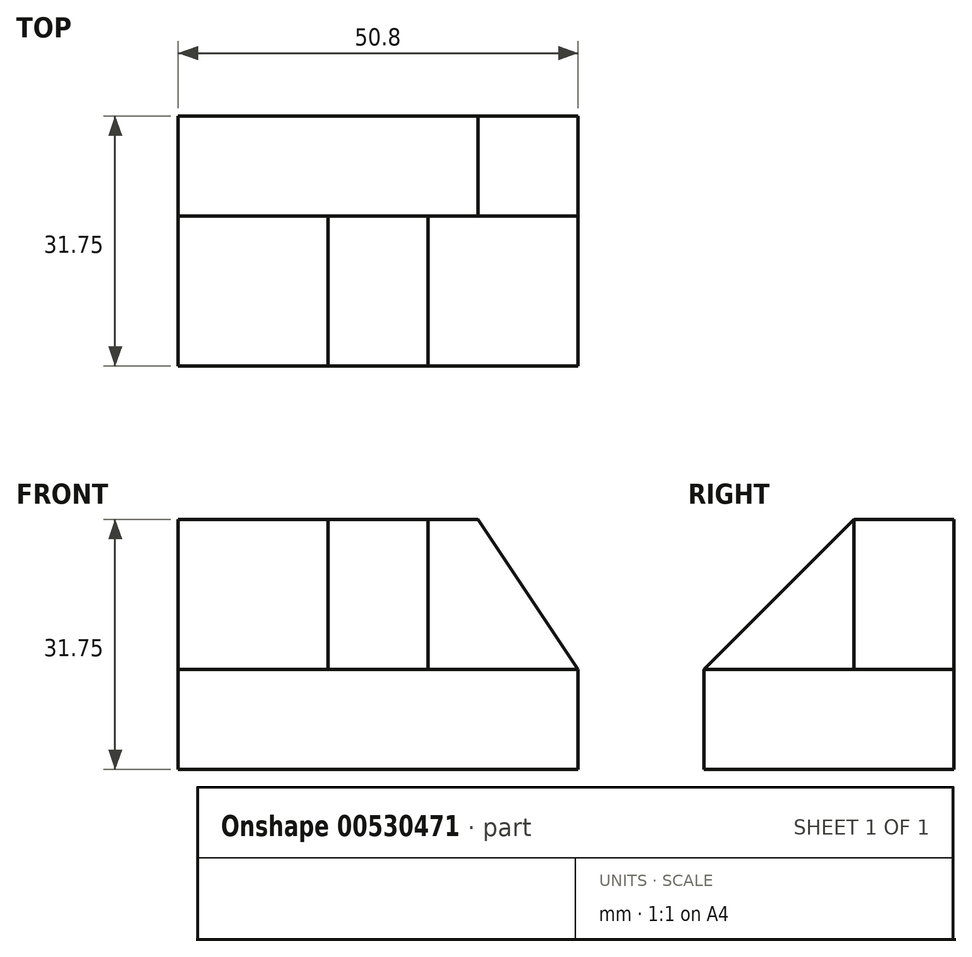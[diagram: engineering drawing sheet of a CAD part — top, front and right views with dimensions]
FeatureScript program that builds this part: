
annotation { "Feature Type Name" : "Feature", "Feature Type Description" : "" }
export const myFeature = defineFeature(function(context is Context, id is Id, definition is map)
    precondition{}
    {
        {
            var Q0;
            Q0=qCreatedBy(makeId("Front.planeOp"),FACE);
            var sketch = newSketch(context, id + "F0", { "sketchPlane" : qUnion([Q0])});
            skLineSegment(sketch, "E0", {"start": v(-85.15, 31.75) * mm, "end": v(-85.15, 0) * mm});
            skLineSegment(sketch, "E1", {"start": v(-85.15, 0) * mm, "end": v(-34.35, 0) * mm});
            skLineSegment(sketch, "E2", {"start": v(-34.35, 0) * mm, "end": v(-34.35, 12.7) * mm});
            skLineSegment(sketch, "E3", {"start": v(-85.15, 31.75) * mm, "end": v(-47.05, 31.75) * mm});
            skLineSegment(sketch, "E4", {"start": v(-47.05, 31.75) * mm, "end": v(-34.35, 12.7) * mm});
            skLineSegment(sketch, "E5", {"start": v(-34.35, 12.7) * mm, "end": v(-85.15, 12.7) * mm});
            skSolve(sketch);
        }
        {
            var Q0;
            {var subQ0=sQuery(id+"F0.wireOp",EDGE,"E1");Q0=makeQuery(id+"F0.imprint","IMPRINT",FACE,{"disambiguationData":[TD([[makeQuery(id+"F0.imprint","IMPRINT",EDGE,{"derivedFrom":subQ0}),1.0]])]});}
            var Q1;
            {var subQ0=sQuery(id+"F0.wireOp",EDGE,"E3");Q1=makeQuery(id+"F0.imprint","IMPRINT",FACE,{"disambiguationData":[TD([[makeQuery(id+"F0.imprint","IMPRINT",EDGE,{"derivedFrom":subQ0}),-1.0]])]});}
            extrude(context, id + "F1", {"entities" : qUnion([Q0, Q1]), "oppositeDirection" : true, "depth" : 31.75 * mm, "offsetDistance" : 25.4 * mm});
        }
        {
            var Q0;
            Q0=makeQuery(id+"F1.opExtrude","CAP_FACE",FACE,{"disambiguationData":[OSD([sQuery(id+"F0.wireOp",EDGE,"E0"),sQuery(id+"F0.wireOp",EDGE,"E1"),sQuery(id+"F0.wireOp",EDGE,"E2"),sQuery(id+"F0.wireOp",EDGE,"E3"),sQuery(id+"F0.wireOp",EDGE,"E4")])],"isStart":true});
            var sketch = newSketch(context, id + "F2", { "sketchPlane" : qUnion([Q0])});
            skLineSegment(sketch, "E6", {"start": v(-34.35, 12.7) * mm, "end": v(-85.15, 12.7) * mm});
            skSolve(sketch);
        }
        {
            var Q0;
            {var subQ0=sQuery(id+"F2.wireOp",EDGE,"E6");Q0=makeQuery(id+"F2.imprint","IMPRINT",FACE,{"disambiguationData":[TD([[makeQuery(id+"F2.imprint","IMPRINT",EDGE,{"derivedFrom":subQ0}),-1.0]])]});}
            extrude(context, id + "F3", {"entities" : qUnion([Q0]), "operationType" : NewBodyOperationType.REMOVE, "oppositeDirection" : true, "depth" : 19.05 * mm, "offsetDistance" : 25.4 * mm});
        }
        {
            var Q0;
            Q0=makeQuery(id+"F3.boolean.opBoolean","COPY",FACE,{"derivedFrom":makeQuery(id+"F3.opExtrude","CAP_FACE",FACE,{"disambiguationData":[OSD([sQuery(id+"F0.wireOp",EDGE,"E0"),sQuery(id+"F0.wireOp",EDGE,"E3"),sQuery(id+"F0.wireOp",EDGE,"E4"),sQuery(id+"F2.wireOp",EDGE,"E6")])],"isStart":false})});
            var sketch = newSketch(context, id + "F4", { "sketchPlane" : qUnion([Q0])});
            skLineSegment(sketch, "E7", {"start": v(-66.1, 31.75) * mm, "end": v(-53.4, 31.75) * mm});
            skLineSegment(sketch, "E8", {"start": v(-53.4, 31.75) * mm, "end": v(-53.4, 12.7) * mm});
            skLineSegment(sketch, "E9", {"start": v(-66.1, 31.75) * mm, "end": v(-66.1, 12.7) * mm});
            skLineSegment(sketch, "E10", {"start": v(-66.1, 12.7) * mm, "end": v(-53.4, 12.7) * mm});
            skLineSegment(sketch, "E11", {"start": v(-53.4, 31.75) * mm, "end": v(-66.1, 31.75) * mm});
            skSolve(sketch);
        }
        {
            var Q0;
            Q0 = qSketchRegion(id + "F4", true);
            extrude(context, id + "F5", {"entities" : qUnion([Q0]), "operationType" : NewBodyOperationType.ADD, "depth" : 19.05 * mm, "offsetDistance" : 25.4 * mm});
        }
        {
            var Q0;
            Q0=makeQuery(id+"F5.opExtrude","SWEPT_FACE",FACE,{"disambiguationData":[OSD([sQuery(id+"F4.wireOp",EDGE,"E8")])]});
            var sketch = newSketch(context, id + "F6", { "sketchPlane" : qUnion([Q0])});
            skLineSegment(sketch, "E12", {"start": v(0, 12.7) * mm, "end": v(19.05, 31.75) * mm});
            skLineSegment(sketch, "E13", {"start": v(19.05, 31.75) * mm, "end": v(0, 31.75) * mm});
            skLineSegment(sketch, "E14", {"start": v(0, 31.75) * mm, "end": v(0, 12.7) * mm});
            skSolve(sketch);
        }
        {
            var Q0;
            Q0=makeQuery(id+"F6.imprint","IMPRINT",FACE,{"disambiguationData":[TD([[makeQuery(id+"F6.imprint","IMPRINT",EDGE,{"derivedFrom":sQuery(id+"F6.wireOp",EDGE,"E12")}),1.0]])]});
            extrude(context, id + "F7", {"entities" : qUnion([Q0]), "operationType" : NewBodyOperationType.REMOVE, "endBound" : BoundingType.THROUGH_ALL, "oppositeDirection" : true, "depth" : 25.4 * mm, "offsetDistance" : 25.4 * mm});
        }
    });
